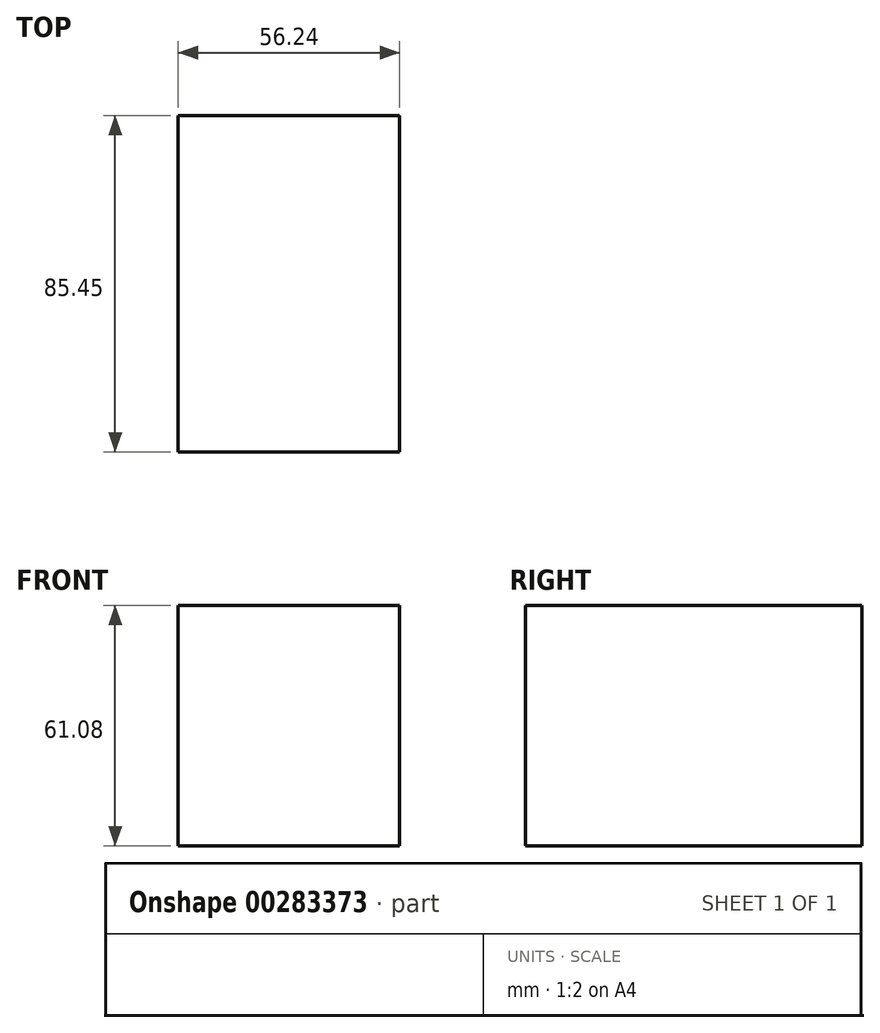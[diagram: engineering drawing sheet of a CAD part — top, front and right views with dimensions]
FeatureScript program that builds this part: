
annotation { "Feature Type Name" : "Feature", "Feature Type Description" : "" }
export const myFeature = defineFeature(function(context is Context, id is Id, definition is map)
    precondition{}
    {
        {
            var Q0;
            Q0=qCreatedBy(makeId("Front.planeOp"),FACE);
            var sketch = newSketch(context, id + "F0", { "sketchPlane" : qUnion([Q0])});
            skLineSegment(sketch, "E0.bottom", {"start": v(0, 0) * mm, "end": v(-68.65, 0) * mm});
            skLineSegment(sketch, "E0.top", {"start": v(0, -64.02) * mm, "end": v(-68.65, -64.02) * mm});
            skLineSegment(sketch, "E0.left", {"start": v(0, 0) * mm, "end": v(0, -64.02) * mm});
            skLineSegment(sketch, "E0.right", {"start": v(-68.65, 0) * mm, "end": v(-68.65, -64.02) * mm});
            skLineSegment(sketch, "E1.bottom", {"start": v(-68.65, 61.08) * mm, "end": v(0, 61.08) * mm});
            skLineSegment(sketch, "E1.top", {"start": v(-68.65, 0) * mm, "end": v(0, 0) * mm});
            skLineSegment(sketch, "E1.left", {"start": v(-68.65, 61.08) * mm, "end": v(-68.65, 0) * mm});
            skLineSegment(sketch, "E1.right", {"start": v(0, 61.08) * mm, "end": v(0, 0) * mm});
            skLineSegment(sketch, "E2.bottom", {"start": v(61.74, -64.02) * mm, "end": v(0, -64.02) * mm});
            skLineSegment(sketch, "E2.top", {"start": v(61.74, 0) * mm, "end": v(0, 0) * mm});
            skLineSegment(sketch, "E2.left", {"start": v(61.74, -64.02) * mm, "end": v(61.74, 0) * mm});
            skLineSegment(sketch, "E2.right", {"start": v(0, -64.02) * mm, "end": v(0, 0) * mm});
            skLineSegment(sketch, "E3.bottom", {"start": v(56.24, 61.08) * mm, "end": v(0, 61.08) * mm});
            skLineSegment(sketch, "E3.top", {"start": v(56.24, 0) * mm, "end": v(0, 0) * mm});
            skLineSegment(sketch, "E3.left", {"start": v(56.24, 61.08) * mm, "end": v(56.24, 0) * mm});
            skSolve(sketch);
        }
        {
            var Q0;
            Q0=makeQuery(id+"F0.imprint","IMPRINT",FACE,{"disambiguationData":[TD([[makeQuery(id+"F0.imprint","IMPRINT",EDGE,{"derivedFrom":sQuery(id+"F0.wireOp",EDGE,"E3.bottom")}),1.0]])]});
            extrude(context, id + "F1", {"entities" : qUnion([Q0]), "depth" : 85.45 * mm});
        }
    });
